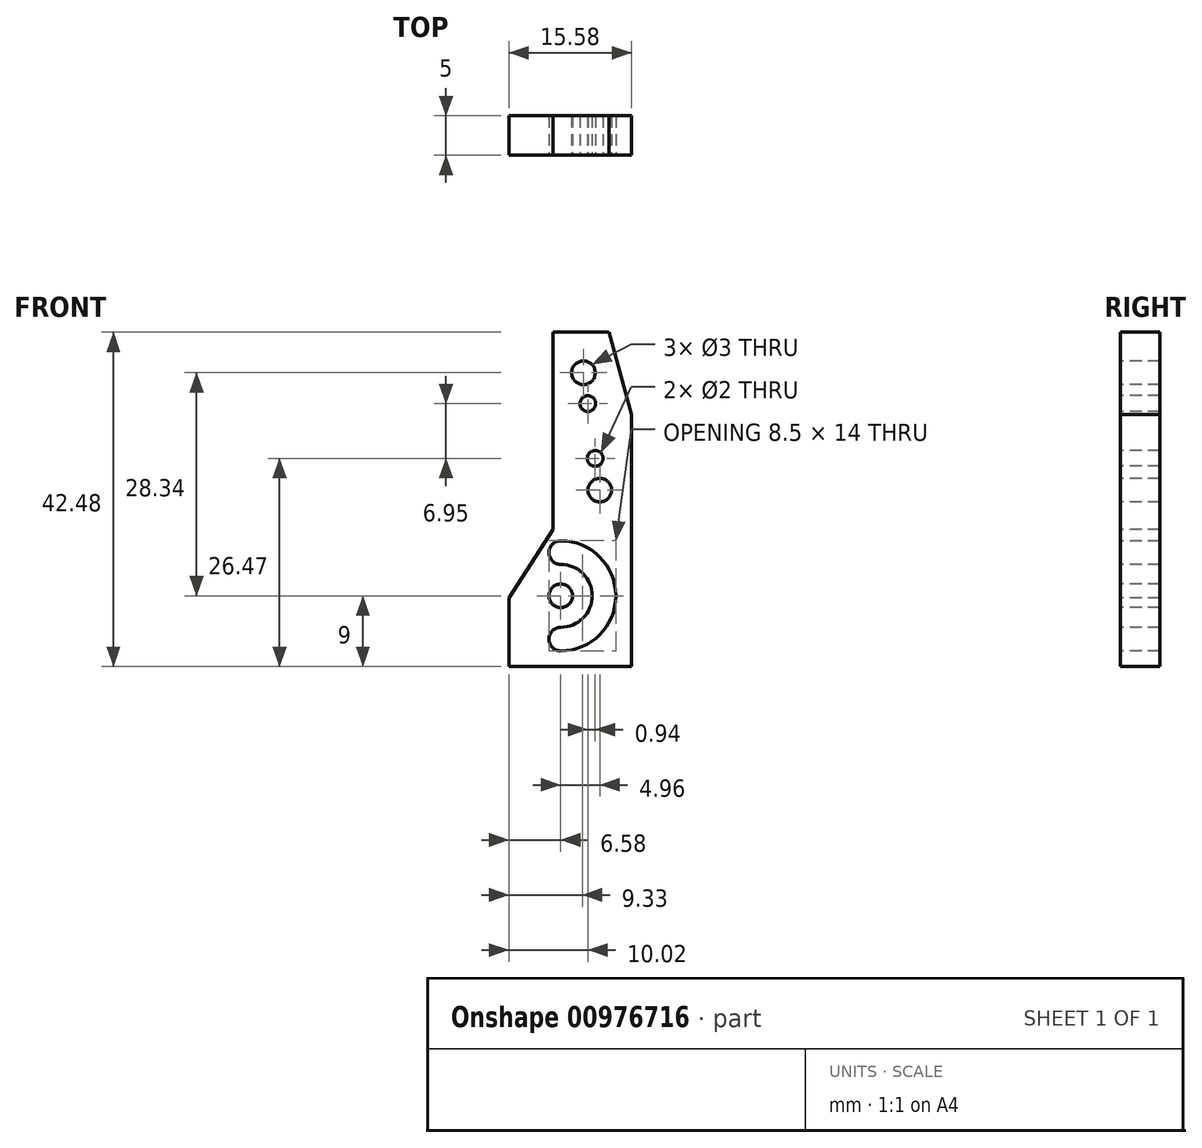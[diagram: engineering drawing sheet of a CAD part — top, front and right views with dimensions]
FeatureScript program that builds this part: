
annotation { "Feature Type Name" : "Feature", "Feature Type Description" : "" }
export const myFeature = defineFeature(function(context is Context, id is Id, definition is map)
    precondition{}
    {
        {
            var Q0;
            Q0=qCreatedBy(makeId("Front.planeOp"),FACE);
            var sketch = newSketch(context, id + "F0", { "sketchPlane" : qUnion([Q0])});
            skLineSegment(sketch, "E0.bottom", {"start": v(7.79, -21.24) * mm, "end": v(-7.8, -21.24) * mm});
            skLineSegment(sketch, "E0.top", {"start": v(7.8, 21.24) * mm, "end": v(-7.79, 21.24) * mm});
            skLineSegment(sketch, "E0.left", {"start": v(7.79, -21.24) * mm, "end": v(7.8, 21.24) * mm});
            skLineSegment(sketch, "E0.right", {"start": v(-7.8, -21.24) * mm, "end": v(-7.8, 21.24) * mm});
            skPoint(sketch, "E0.middle", {"position": v(0, 0) * mm});
            skSolve(sketch);
        }
        {
            var Q0;
            Q0 = qSketchRegion(id + "F0", true);
            extrude(context, id + "F1", {"entities" : qUnion([Q0]), "oppositeDirection" : true, "depth" : 5 * mm, "offsetDistance" : 25 * mm});
        }
        {
            var Q0;
            Q0=makeQuery(id+"F1.opExtrude","CAP_FACE",FACE,{"disambiguationData":[OSD([sQuery(id+"F0.wireOp",EDGE,"E0.bottom"),sQuery(id+"F0.wireOp",EDGE,"E0.top"),sQuery(id+"F0.wireOp",EDGE,"E0.left"),sQuery(id+"F0.wireOp",EDGE,"E0.right")])],"isStart":true});
            var sketch = newSketch(context, id + "F2", { "sketchPlane" : qUnion([Q0])});
            skLineSegment(sketch, "E1", {"start": v(7.79, -21.24) * mm, "end": v(7.8, 10.8) * mm});
            skLineSegment(sketch, "E2", {"start": v(7.79, 10.8) * mm, "end": v(4.9, 21.24) * mm});
            skLineSegment(sketch, "E3", {"start": v(7.8, 10.8) * mm, "end": v(7.8, 21.24) * mm});
            skLineSegment(sketch, "E4", {"start": v(7.8, 21.24) * mm, "end": v(4.9, 21.24) * mm});
            skSolve(sketch);
        }
        {
            var Q0;
            Q0 = qSketchRegion(id + "F2", true);
            extrude(context, id + "F3", {"entities" : qUnion([Q0]), "operationType" : NewBodyOperationType.REMOVE, "endBound" : BoundingType.UP_TO_NEXT, "oppositeDirection" : true, "depth" : 25 * mm, "offsetDistance" : 25 * mm});
        }
        {
            var Q0;
            Q0=makeQuery(id+"F1.opExtrude","CAP_FACE",FACE,{"disambiguationData":[OSD([sQuery(id+"F0.wireOp",EDGE,"E0.bottom"),sQuery(id+"F0.wireOp",EDGE,"E0.top"),sQuery(id+"F0.wireOp",EDGE,"E0.left"),sQuery(id+"F0.wireOp",EDGE,"E0.right")])],"isStart":true});
            var sketch = newSketch(context, id + "F4", { "sketchPlane" : qUnion([Q0])});
            skLineSegment(sketch, "E5", {"start": v(4.9, 21.24) * mm, "end": v(-2.19, 21.24) * mm});
            skLineSegment(sketch, "E6", {"start": v(-2.19, 21.24) * mm, "end": v(-2.19, -3.8) * mm});
            skLineSegment(sketch, "E7.top", {"start": v(-2.19, 21.24) * mm, "end": v(-7.8, 21.24) * mm});
            skLineSegment(sketch, "E7.left", {"start": v(-2.19, -3.8) * mm, "end": v(-2.19, 21.24) * mm});
            skLineSegment(sketch, "E8", {"start": v(-7.8, -21.24) * mm, "end": v(-7.8, -12.51) * mm});
            skLineSegment(sketch, "E9", {"start": v(-7.8, -12.51) * mm, "end": v(-2.2, -3.8) * mm});
            skLineSegment(sketch, "E10", {"start": v(-7.8, 21.24) * mm, "end": v(-7.8, -12.51) * mm});
            skSolve(sketch);
        }
        {
            var Q0;
            Q0 = qSketchRegion(id + "F4", true);
            extrude(context, id + "F5", {"entities" : qUnion([Q0]), "operationType" : NewBodyOperationType.REMOVE, "endBound" : BoundingType.UP_TO_NEXT, "oppositeDirection" : true, "depth" : 25 * mm, "offsetDistance" : 25 * mm});
        }
        {
            var Q0;
            Q0=makeQuery(id+"F1.opExtrude","CAP_FACE",FACE,{"disambiguationData":[OSD([sQuery(id+"F0.wireOp",EDGE,"E0.bottom"),sQuery(id+"F0.wireOp",EDGE,"E0.top"),sQuery(id+"F0.wireOp",EDGE,"E0.left"),sQuery(id+"F0.wireOp",EDGE,"E0.right")])],"isStart":true});
            var sketch = newSketch(context, id + "F6", { "sketchPlane" : qUnion([Q0])});
            skLineSegment(sketch, "E11", {"start": v(7.79, -21.24) * mm, "end": v(7.8, 1.2) * mm});
            skLineSegment(sketch, "E12", {"start": v(7.79, 1.2) * mm, "end": v(3.75, 1.2) * mm});
            skLineSegment(sketch, "E13", {"start": v(7.79, -21.24) * mm, "end": v(7.79, 5.23) * mm});
            skLineSegment(sketch, "E14", {"start": v(7.79, 5.23) * mm, "end": v(3.17, 5.23) * mm});
            skLineSegment(sketch, "E15", {"start": v(7.79, -21.24) * mm, "end": v(7.79, 12.18) * mm});
            skLineSegment(sketch, "E16", {"start": v(7.79, 12.18) * mm, "end": v(2.23, 12.18) * mm});
            skLineSegment(sketch, "E17", {"start": v(7.79, -21.24) * mm, "end": v(7.79, 16.1) * mm});
            skLineSegment(sketch, "E18", {"start": v(7.79, 16.1) * mm, "end": v(1.68, 16.1) * mm});
            skCircle(sketch, "E19", {"center": v(3.75, 1.2) * mm, "radius": 1.5 * mm});
            skCircle(sketch, "E20", {"center": v(3.17, 5.23) * mm, "radius": 1 * mm});
            skCircle(sketch, "E21", {"center": v(2.23, 12.18) * mm, "radius": 1 * mm});
            skCircle(sketch, "E22", {"center": v(1.68, 16.1) * mm, "radius": 1.5 * mm});
            skSolve(sketch);
        }
        {
            var Q0;
            Q0 = qSketchRegion(id + "F6", true);
            extrude(context, id + "F7", {"entities" : qUnion([Q0]), "operationType" : NewBodyOperationType.REMOVE, "endBound" : BoundingType.UP_TO_NEXT, "oppositeDirection" : true, "depth" : 25 * mm, "offsetDistance" : 25 * mm});
        }
        {
            var Q0;
            Q0=makeQuery(id+"F1.opExtrude","CAP_FACE",FACE,{"disambiguationData":[OSD([sQuery(id+"F0.wireOp",EDGE,"E0.bottom"),sQuery(id+"F0.wireOp",EDGE,"E0.top"),sQuery(id+"F0.wireOp",EDGE,"E0.left"),sQuery(id+"F0.wireOp",EDGE,"E0.right")])],"isStart":true});
            var sketch = newSketch(context, id + "F8", { "sketchPlane" : qUnion([Q0])});
            skLineSegment(sketch, "E23", {"start": v(7.79, -21.24) * mm, "end": v(-1.21, -21.24) * mm});
            skLineSegment(sketch, "E24", {"start": v(-1.21, -21.24) * mm, "end": v(-1.21, -12.24) * mm});
            skCircle(sketch, "E25", {"center": v(-1.21, -12.24) * mm, "radius": 1.5 * mm});
            skLineSegment(sketch, "E26", {"start": v(-1.21, -8.24) * mm, "end": v(-1.21, -6.74) * mm});
            skLineSegment(sketch, "E27", {"start": v(-1.21, -6.74) * mm, "end": v(-1.21, -5.24) * mm});
            skLineSegment(sketch, "E28", {"start": v(-1.21, -12.24) * mm, "end": v(-1.21, -16.74) * mm});
            skLineSegment(sketch, "E29", {"start": v(-1.21, -12.24) * mm, "end": v(-1.21, -16.24) * mm});
            skLineSegment(sketch, "E30", {"start": v(-1.21, -16.24) * mm, "end": v(-1.21, -17.74) * mm});
            skLineSegment(sketch, "E31", {"start": v(-1.21, -17.74) * mm, "end": v(-1.21, -19.24) * mm});
            skArc(sketch, "E32", {"start": v(-1.21, -16.24) * mm, "mid": v(2.79, -12.24) * mm, "end": v(-1.21, -8.24) * mm});
            skArc(sketch, "E33", {"start": v(-1.21, -19.24) * mm, "mid": v(5.79, -12.24) * mm, "end": v(-1.21, -5.24) * mm});
            skArc(sketch, "E34", {"start": v(-1.21, -16.24) * mm, "mid": v(-2.71, -17.74) * mm, "end": v(-1.21, -19.24) * mm});
            skArc(sketch, "E35", {"start": v(-1.21, -5.24) * mm, "mid": v(-2.71, -6.74) * mm, "end": v(-1.21, -8.24) * mm});
            skSolve(sketch);
        }
        {
            var Q0;
            Q0 = qSketchRegion(id + "F8", true);
            extrude(context, id + "F9", {"entities" : qUnion([Q0]), "operationType" : NewBodyOperationType.REMOVE, "endBound" : BoundingType.UP_TO_NEXT, "oppositeDirection" : true, "depth" : 25 * mm, "offsetDistance" : 25 * mm});
        }
    });
